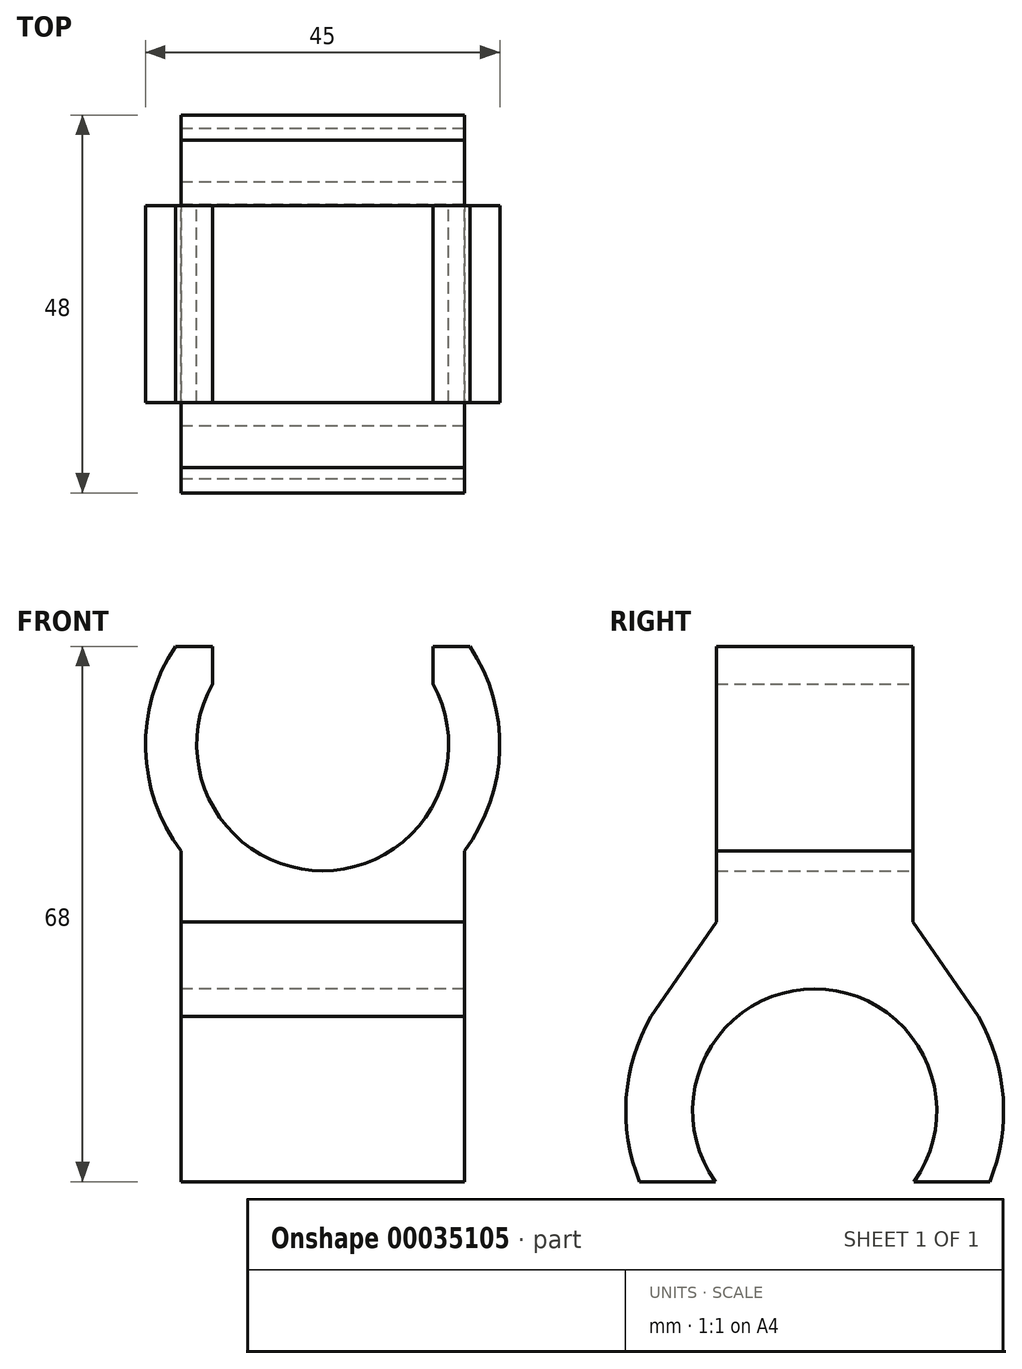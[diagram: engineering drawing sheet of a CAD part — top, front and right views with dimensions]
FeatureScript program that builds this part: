
annotation { "Feature Type Name" : "Feature", "Feature Type Description" : "" }
export const myFeature = defineFeature(function(context is Context, id is Id, definition is map)
    precondition{}
    {
        {
            var Q0;
            Q0=qCreatedBy(makeId("Front.planeOp"),FACE);
            var sketch = newSketch(context, id + "F0", { "sketchPlane" : qUnion([Q0])});
            skArc(sketch, "E0", {"start": v(-14, 30.25) * mm, "mid": v(0, 6.5) * mm, "end": v(14, 30.25) * mm});
            skLineSegment(sketch, "E1", {"start": v(-18.7, 35) * mm, "end": v(-14, 35) * mm});
            skArc(sketch, "E2", {"start": v(-18.7, 35) * mm, "mid": v(0, 0) * mm, "end": v(18.7, 35) * mm});
            skLineSegment(sketch, "E3.trimOffspring", {"start": v(14, 35) * mm, "end": v(18.7, 35) * mm});
            skLineSegment(sketch, "E4", {"start": v(-18, 9) * mm, "end": v(-18, 0) * mm});
            skLineSegment(sketch, "E5", {"start": v(-18, 0) * mm, "end": v(0, 0) * mm});
            skLineSegment(sketch, "E6.MirrorCS", {"start": v(18, 9) * mm, "end": v(18, 0) * mm});
            skLineSegment(sketch, "E7.MirrorCS", {"start": v(18, 0) * mm, "end": v(0, 0) * mm});
            skLineSegment(sketch, "E8", {"start": v(-14, 30.25) * mm, "end": v(-14, 35) * mm});
            skLineSegment(sketch, "E9.MirrorCS", {"start": v(14, 30.25) * mm, "end": v(14, 35) * mm});
            skPoint(sketch, "E10.orphan", {"position": v(-14, 34.9) * mm});
            skPoint(sketch, "E11.orphan", {"position": v(-14, 31.7) * mm});
            skPoint(sketch, "E12.orphan", {"position": v(14, 34.9) * mm});
            skPoint(sketch, "E13.orphan", {"position": v(14, 31.7) * mm});
            skSolve(sketch);
        }
        {
            var Q0;
            {var subQ1=sQuery(id+"F0.wireOp",EDGE,"E4");Q0=makeQuery(id+"F0.imprint","IMPRINT",FACE,{"disambiguationData":[TD([[makeQuery(id+"F0.imprint","IMPRINT",EDGE,{"derivedFrom":subQ1}),1.0]])]});}
            var Q1;
            Q1=makeQuery(id+"F0.imprint","IMPRINT",FACE,{"disambiguationData":[TD([[makeQuery(id+"F0.imprint","IMPRINT",EDGE,{"derivedFrom":sQuery(id+"F0.wireOp",EDGE,"E0")}),-1.0]])]});
            var Q2;
            {var subQ1=sQuery(id+"F0.wireOp",EDGE,"E6.MirrorCS");Q2=makeQuery(id+"F0.imprint","IMPRINT",FACE,{"disambiguationData":[TD([[makeQuery(id+"F0.imprint","IMPRINT",EDGE,{"derivedFrom":subQ1}),-1.0]])]});}
            extrude(context, id + "F1", {"entities" : qUnion([Q0, Q1, Q2]), "endBound" : BoundingType.SYMMETRIC, "depth" : 25 * mm});
        }
        {
            var Q0;
            Q0=qCreatedBy(makeId("Right.planeOp"),FACE);
            var sketch = newSketch(context, id + "F2", { "sketchPlane" : qUnion([Q0])});
            skLineSegment(sketch, "E14", {"start": v(-12.62, -33) * mm, "end": v(-22.25, -33) * mm});
            skLineSegment(sketch, "E15.MirrorCS", {"start": v(12.62, -33) * mm, "end": v(22.25, -33) * mm});
            skPoint(sketch, "E16.orphan", {"position": v(0, -33) * mm});
            skArc(sketch, "E17", {"start": v(12.62, -33) * mm, "mid": v(0, -8.5) * mm, "end": v(-12.62, -33) * mm});
            skArc(sketch, "E18", {"start": v(22.25, -33) * mm, "mid": v(0, 0) * mm, "end": v(-22.25, -33) * mm});
            skLineSegment(sketch, "E19", {"start": v(20.78, -12) * mm, "end": v(12.5, 0) * mm});
            skLineSegment(sketch, "E20.MirrorCS", {"start": v(-20.78, -12) * mm, "end": v(-12.5, 0) * mm});
            skLineSegment(sketch, "E21", {"start": v(-12.5, 0) * mm, "end": v(0, 0) * mm});
            skLineSegment(sketch, "E22.MirrorCS", {"start": v(12.5, 0) * mm, "end": v(0, 0) * mm});
            skSolve(sketch);
        }
        {
            var Q0;
            {var subQ7=sQuery(id+"F2.wireOp",EDGE,"E14");Q0=makeQuery(id+"F2.imprint","IMPRINT",FACE,{"disambiguationData":[TD([[makeQuery(id+"F2.imprint","IMPRINT",EDGE,{"derivedFrom":subQ7}),-1.0]])]});}
            var Q1;
            {var subQ0=sQuery(id+"F2.wireOp",EDGE,"E21");Q1=makeQuery(id+"F2.imprint","IMPRINT",FACE,{"disambiguationData":[TD([[makeQuery(id+"F2.imprint","IMPRINT",EDGE,{"derivedFrom":subQ0}),-1.0]])]});}
            var Q2;
            {var subQ0=sQuery(id+"F2.wireOp",EDGE,"E22.MirrorCS");Q2=makeQuery(id+"F2.imprint","IMPRINT",FACE,{"disambiguationData":[TD([[makeQuery(id+"F2.imprint","IMPRINT",EDGE,{"derivedFrom":subQ0}),1.0]])]});}
            extrude(context, id + "F3", {"entities" : qUnion([Q0, Q1, Q2]), "operationType" : NewBodyOperationType.ADD, "endBound" : BoundingType.SYMMETRIC, "depth" : 36 * mm});
        }
    });
